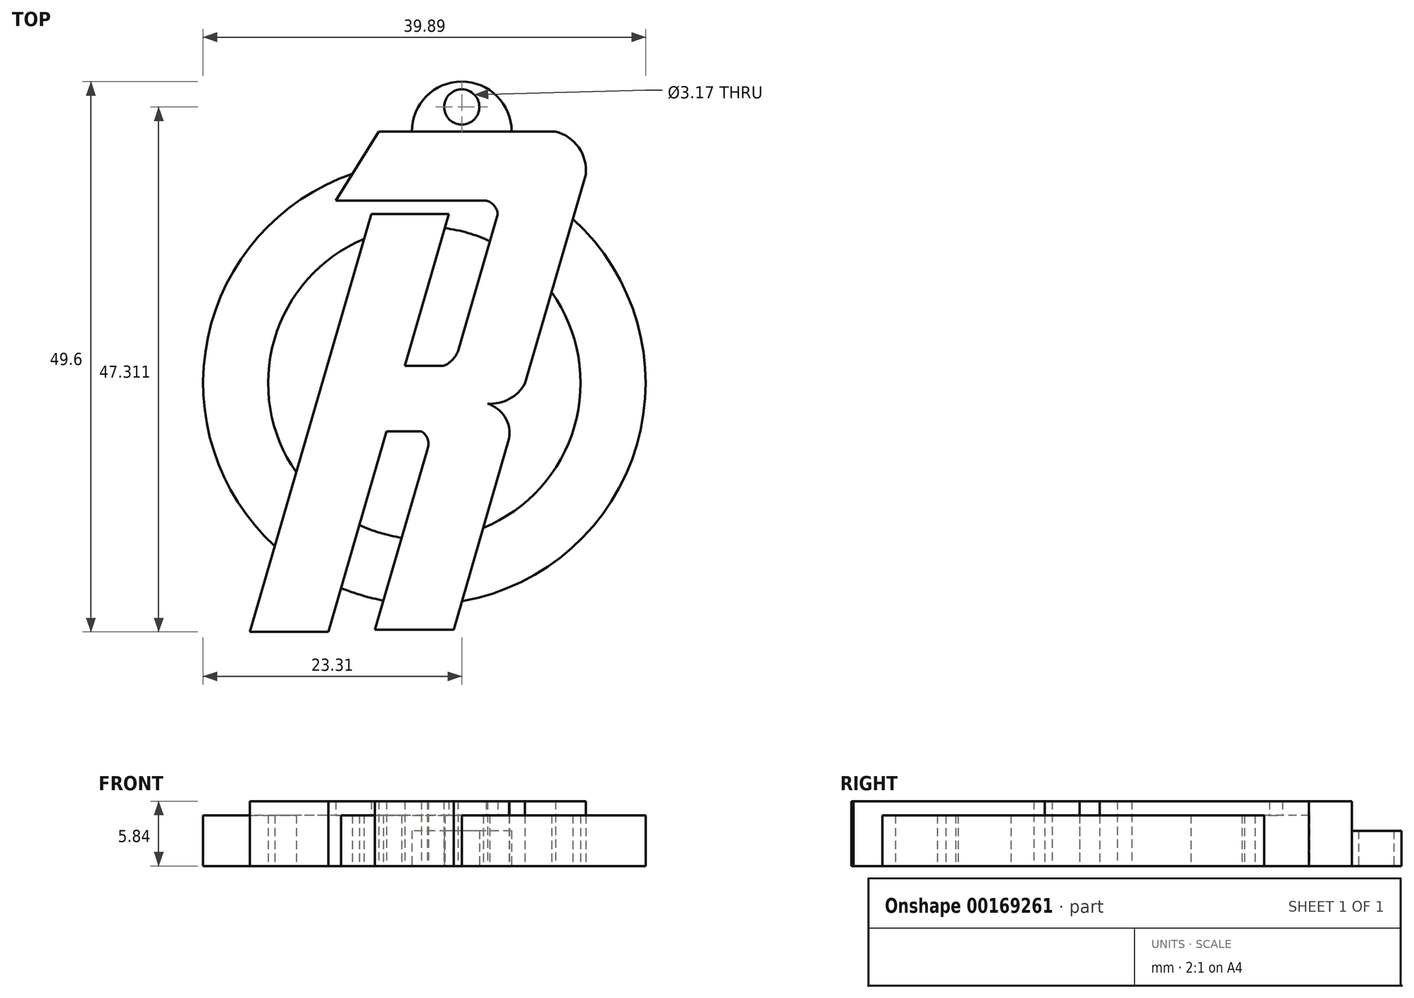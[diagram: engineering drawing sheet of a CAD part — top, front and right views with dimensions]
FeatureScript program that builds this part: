
annotation { "Feature Type Name" : "Feature", "Feature Type Description" : "" }
export const myFeature = defineFeature(function(context is Context, id is Id, definition is map)
    precondition{}
    {
        {
            var Q0;
            Q0=qCreatedBy(makeId("Top.planeOp"),FACE);
            var sketch = newSketch(context, id + "F0", { "sketchPlane" : qUnion([Q0])});
            skLineSegment(sketch, "E0", {"start": v(-7.48, 18.82) * mm, "end": v(-11.35, 12.6) * mm});
            skLineSegment(sketch, "E1", {"start": v(-11.35, 12.6) * mm, "end": v(2.2, 12.6) * mm});
            skLineSegment(sketch, "E2", {"start": v(3.25, 11.4) * mm, "end": v(-0.35, -1) * mm});
            skLineSegment(sketch, "E3", {"start": v(-1.6, -2.3) * mm, "end": v(-5.13, -2.3) * mm});
            skLineSegment(sketch, "E4", {"start": v(-5.13, -2.3) * mm, "end": v(-1.15, 11.4) * mm});
            skLineSegment(sketch, "E5", {"start": v(-1.15, 11.4) * mm, "end": v(-8.16, 11.4) * mm});
            skLineSegment(sketch, "E6", {"start": v(-8.16, 11.4) * mm, "end": v(-19.1, -26.28) * mm});
            skLineSegment(sketch, "E7", {"start": v(-19.1, -26.28) * mm, "end": v(-12.03, -26.28) * mm});
            skLineSegment(sketch, "E8", {"start": v(-12.03, -26.28) * mm, "end": v(-6.78, -8.19) * mm});
            skLineSegment(sketch, "E9", {"start": v(-6.78, -8.19) * mm, "end": v(-3.64, -8.19) * mm});
            skLineSegment(sketch, "E10", {"start": v(-3.01, -9.52) * mm, "end": v(-7.82, -26.08) * mm});
            skLineSegment(sketch, "E11", {"start": v(-7.82, -26.08) * mm, "end": v(-0.73, -26.08) * mm});
            skLineSegment(sketch, "E12", {"start": v(-0.73, -26.08) * mm, "end": v(4.28, -8.84) * mm});
            skLineSegment(sketch, "E13", {"start": v(8.45, 18.82) * mm, "end": v(-7.48, 18.82) * mm});
            skArc(sketch, "E14", {"start": v(11.18, 14.95) * mm, "mid": v(10.54, 17.4) * mm, "end": v(8.45, 18.82) * mm});
            skArc(sketch, "E15", {"start": v(3.25, 11.4) * mm, "mid": v(2.9, 12.16) * mm, "end": v(2.2, 12.6) * mm});
            skPoint(sketch, "E16.orphan", {"position": v(12.3, 18.82) * mm});
            skArc(sketch, "E17", {"start": v(2.33, -5.7) * mm, "mid": v(4.28, -5.29) * mm, "end": v(5.7, -3.9) * mm});
            skArc(sketch, "E18", {"start": v(4.28, -8.84) * mm, "mid": v(3.89, -6.9) * mm, "end": v(2.33, -5.7) * mm});
            skLineSegment(sketch, "E19.trimOffspring", {"start": v(5.7, -3.9) * mm, "end": v(11.18, 14.95) * mm});
            skArc(sketch, "E20", {"start": v(-1.6, -2.3) * mm, "mid": v(-0.86, -1.77) * mm, "end": v(-0.35, -1) * mm});
            skPoint(sketch, "E21.orphan", {"position": v(-0.73, -2.3) * mm});
            skArc(sketch, "E22", {"start": v(-3.1, -9.85) * mm, "mid": v(-3.06, -8.92) * mm, "end": v(-3.64, -8.19) * mm});
            skArc(sketch, "E23", {"start": v(-9.85, 15.01) * mm, "mid": v(-22.9, 0.23) * mm, "end": v(-16.85, -18.54) * mm});
            skPoint(sketch, "E23.centerSnap0", {"position": v(-3.37, -2.3) * mm});
            skArc(sketch, "E24", {"start": v(-8.82, 9.14) * mm, "mid": v(-16.9, 0.08) * mm, "end": v(-14.92, -11.9) * mm});
            skArc(sketch, "E25.trimOffspring", {"start": v(2.53, 8.94) * mm, "mid": v(0.55, 9.68) * mm, "end": v(-1.52, 10.11) * mm});
            skArc(sketch, "E26.trimOffspring", {"start": v(1.94, -16.9) * mm, "mid": v(10.16, -7.77) * mm, "end": v(8.1, 4.33) * mm});
            skArc(sketch, "E27.trimOffspring", {"start": v(-9.24, -16.65) * mm, "mid": v(-7.36, -17.35) * mm, "end": v(-5.4, -17.78) * mm});
            skArc(sketch, "E28.trimOffspring", {"start": v(-10.88, -22.32) * mm, "mid": v(-9, -22.98) * mm, "end": v(-7.05, -23.45) * mm});
            skArc(sketch, "E29.trimOffspring", {"start": v(0.02, -23.5) * mm, "mid": v(15.78, -9.4) * mm, "end": v(10.02, 10.94) * mm});
            skPoint(sketch, "E30.centerSnap0", {"position": v(0.49, 18.82) * mm});
            skCircle(sketch, "E31", {"center": v(0, 21.03) * mm, "radius": 1.59 * mm});
            skArc(sketch, "E32", {"start": v(4.5, 18.82) * mm, "mid": v(0, 23.32) * mm, "end": v(-4.5, 18.82) * mm});
            skSolve(sketch);
        }
        {
            var Q0;
            {var subQ27=sQuery(id+"F0.wireOp",EDGE,"E1");Q0=makeQuery(id+"F0.imprint","IMPRINT",FACE,{"disambiguationData":[TD([[makeQuery(id+"F0.imprint","IMPRINT",EDGE,{"derivedFrom":subQ27}),1.0]])]});}
            extrude(context, id + "F1", {"entities" : qUnion([Q0]), "depth" : 5.84 * mm});
        }
        {
            var Q0;
            {var subQ4=sQuery(id+"F0.wireOp",EDGE,"E1");Q0=makeQuery(id+"F0.imprint","IMPRINT",FACE,{"disambiguationData":[TD([[makeQuery(id+"F0.imprint","IMPRINT",EDGE,{"derivedFrom":subQ4}),-1.0]])]});}
            var Q1;
            {var subQ0=sQuery(id+"F0.wireOp",EDGE,"E26.trimOffspring");Q1=makeQuery(id+"F0.imprint","IMPRINT",FACE,{"disambiguationData":[TD([[makeQuery(id+"F0.imprint","IMPRINT",EDGE,{"derivedFrom":subQ0}),-1.0]])]});}
            var Q2;
            {var subQ0=sQuery(id+"F0.wireOp",EDGE,"E27.trimOffspring");Q2=makeQuery(id+"F0.imprint","IMPRINT",FACE,{"disambiguationData":[TD([[makeQuery(id+"F0.imprint","IMPRINT",EDGE,{"derivedFrom":subQ0}),-1.0]])]});}
            extrude(context, id + "F2", {"entities" : qUnion([Q0, Q1, Q2]), "operationType" : NewBodyOperationType.ADD, "depth" : 4.57 * mm});
        }
        {
            var Q0;
            Q0=makeQuery(id+"F0.imprint","IMPRINT",FACE,{"disambiguationData":[TD([[makeQuery(id+"F0.imprint","IMPRINT",EDGE,{"derivedFrom":sQuery(id+"F0.wireOp",EDGE,"E31")}),-1.0]])]});
            extrude(context, id + "F3", {"entities" : qUnion([Q0]), "operationType" : NewBodyOperationType.ADD, "depth" : 3.17 * mm});
        }
    });
